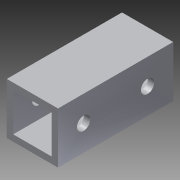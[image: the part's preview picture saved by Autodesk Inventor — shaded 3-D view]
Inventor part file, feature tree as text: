
AUTODESK INVENTOR PART (.ipt)
format: ipt  version: 2014 SP1 (Build 180222100, 222)  size: 97,792 bytes
history: native  units: in
note: dims shown in document units (in); Inventor stores cm internally (conversion verified against a paired STEP export)
features: extrude x2, sketch x2
ambient origin geometry x8: Origin, YZ Plane, XZ Plane, XY Plane, X Axis, Y Axis, Z Axis, Center Point
bodies: Solid1 (feature_tree)
feature tree (4):
  extrude  "Extrusion1"  Depth=1.0in
  extrude  "Extrusion2"  Depth=2.25in TaperAngle=0.0deg
  sketch  "Sketch1"  dims[d0=1.0in d1=1.0in]
  sketch  "Sketch2"  dims[d2=0.125in d3=2.25in d4=0.0in d5=1.25in d7=0.5in d8=0.26in d9=2.25in d10=0.0in]
